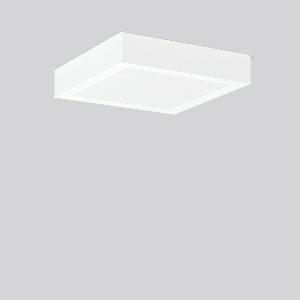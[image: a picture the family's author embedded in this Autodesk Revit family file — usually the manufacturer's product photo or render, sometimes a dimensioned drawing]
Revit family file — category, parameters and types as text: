
# Revit family: toledo_flat_square_a_672277_002_07_d847
name_source: partatom
category: Lighting Fixtures
units: mm (PartAtom-declared; Revit-internal decimal feet)

## family parameters
Cut with Voids When Loaded = No
Host = Face
Light Source = No
Part Type = Normal
Room Calculation Point = No
Round Connector Dimension = Use Diameter
Shared = No

## types (1)
- TOLEDO FLAT square A (1 x LED Modul 830, 2050 lm, 3000)
    Apparent Load = 25 VA
    CIE Flux Codes = 48 80 96 100 100
    Color Rendering = 80
    Color Temperature = 3000
    Default Elevation = 1800 mm
    Description = Series: TOLEDO FLAT square
Ultra thin surface mounted downlight. For escape route illumination. Surface mounted housing: sheet steel, powder-coated. Square cover plate: die-cast aluminium, powder coated. Light guide and diffuser made of non-yellowing PMMA, opal matt. Self-contained system with automatic self-test and feedback via DALI bus, only to RZB DALI monitoring system. 
Colour: white
Length: 300 mm
Width: 300 mm
Height: 58 mm
Weight: 3.96 kg
Operating mode: maintained power mode
Duration time: 3 h
Lamp: LED
Socket: without socket
Colour temperature: 3000K
Colour rendering index (CRI): 80
System power: 25 W
Rated luminous flux: 2050 lm
Luminous flux, emergency: 420 lm
System power, emergency: -
Control gear: Regulated power supply
Protection class: I
Type of protection: IP 40
    Height = 58 mm
    Lamp = 1 x LED Modul 830
    Lamp Light Flux = 2050 lm
    Lamp count = 1
    Length = 300 mm
    Lifetime = 50000 h
    Luminous efficacy = 82 lm/W
    Manufacturer = RZB
    ModVariant = No
    Model = 672277.002.07
    Mounting Place = Ceiling
    Mounting Type = Surface mounted
    Number of Poles = 1
    OnlyDefault = Yes
    Power Factor = 1
    Product Name = TOLEDO FLAT square A
    Product group = Surface mounted downlights
    ProductGroupID = 302
    Protection Class = Protection class I
    Protection Degree = IP 40
    RLX_Detail_Level = 1
    RLX_Emergency_Light_Flux = 420 lm
    RLX_Emergency_Type = 3
    RLX_Emergency_Type_DB = Yes
    RlxData = <blob elided: 14041 chars, md5=7dea5b43>
    Socket = socket
    Standby Power = 0 W
    System Light Flux = 2050 lm
    System Power = 25 W
    Type Comments = Product without accessories
    Type Image = 901554.002.jpg
    URL = http://relux.com
    VarID = ---
    Voltage = 0 V
    Weight = 0.00 kg
    Width = 300 mm

## geometry (parser evidence)
native form markers: Sweep x13
no freeform markers — native parametric forms only
